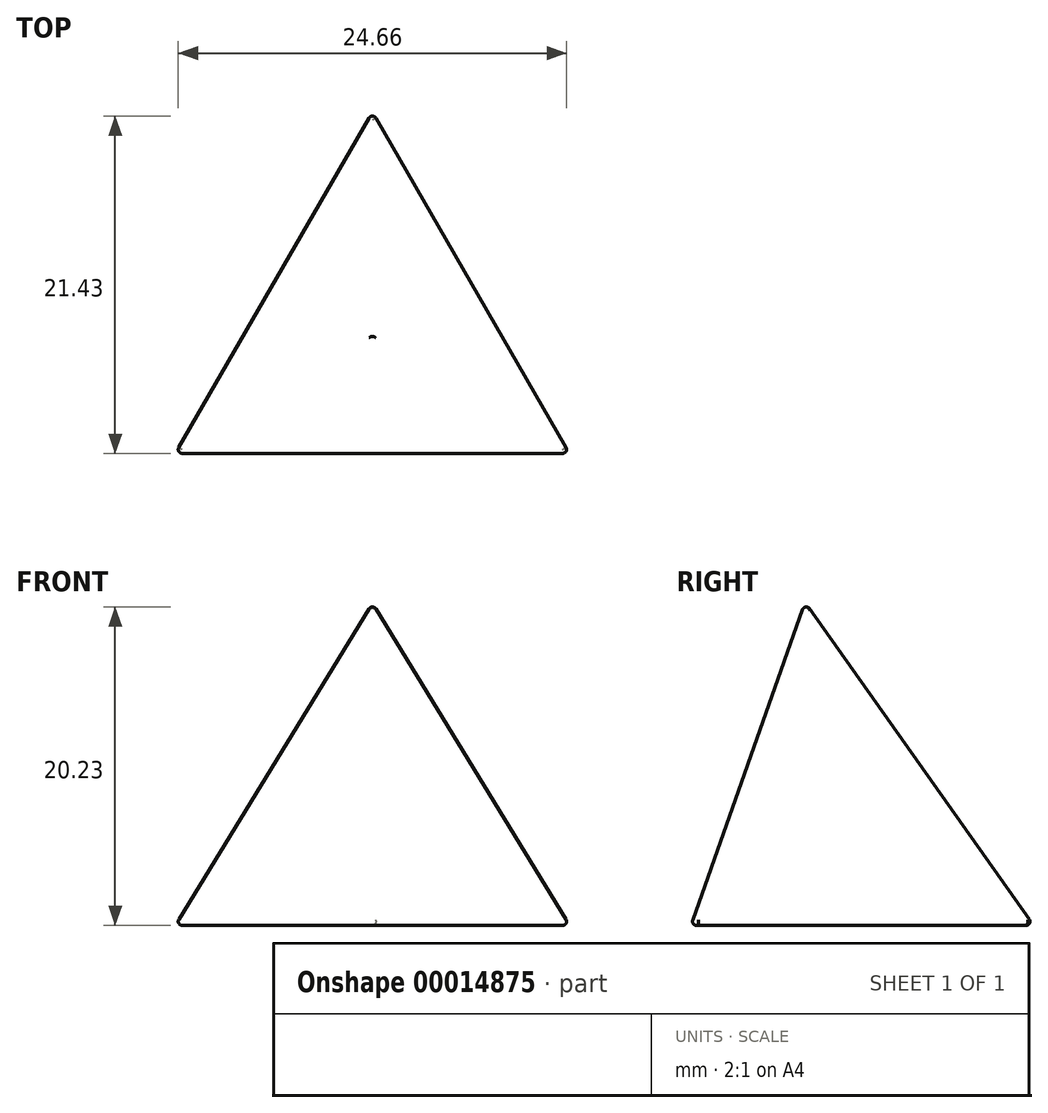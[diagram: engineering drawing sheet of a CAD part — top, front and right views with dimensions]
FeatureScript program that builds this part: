
annotation { "Feature Type Name" : "Feature", "Feature Type Description" : "" }
export const myFeature = defineFeature(function(context is Context, id is Id, definition is map)
    precondition{}
    {
        {
            var Q0;
            Q0=qCreatedBy(makeId("Top.planeOp"),FACE);
            var sketch = newSketch(context, id + "F0", { "sketchPlane" : qUnion([Q0])});
            skLineSegment(sketch, "E0", {"start": v(-12.7, -7.33) * mm, "end": v(12.7, -7.33) * mm, "construction": true});
            skLineSegment(sketch, "E1", {"start": v(12.7, -7.33) * mm, "end": v(0, 14.66) * mm, "construction": true});
            skLineSegment(sketch, "E2", {"start": v(0, 14.66) * mm, "end": v(-12.7, -7.33) * mm, "construction": true});
            skCircle(sketch, "E3", {"center": v(0, 0) * mm, "radius": 14.66 * mm});
            skLineSegment(sketch, "E4", {"start": v(-12.7, -7.33) * mm, "end": v(0, 0) * mm, "construction": true});
            skCircle(sketch, "E5", {"center": v(-12.7, -7.33) * mm, "radius": 25.4 * mm, "construction": true});
            skLineSegment(sketch, "E6", {"start": v(-12.7, -7.33) * mm, "end": v(-34.7, -20.03) * mm, "construction": true});
            skSolve(sketch);
        }
        {
            var Q0;
            Q0=sQuery(id+"F0.wireOp",EDGE,"E4");
            cPlane(context, id + "F1", {"entities" : qUnion([Q0]), "cplaneType" : CPlaneType.LINE_ANGLE, "offset" : 152.4 * mm, "angle" : 0 * degree, "width" : 152.4 * mm, "height" : 152.4 * mm});
        }
        {
            var Q0;
            Q0=qCreatedBy(id+"F1.planeOp",FACE);
            var sketch = newSketch(context, id + "F2", { "sketchPlane" : qUnion([Q0])});
            skLineSegment(sketch, "E7", {"start": v(14.66, 0) * mm, "end": v(0, 20.74) * mm, "construction": true});
            skLineSegment(sketch, "E8", {"start": v(0, 20.74) * mm, "end": v(0, 0) * mm, "construction": true});
            skSolve(sketch);
        }
        {
            var Q0;
            Q0=sQuery(id+"F0.wireOp",VERTEX,"E1.end");
            var Q1;
            Q1=sQuery(id+"F0.wireOp",VERTEX,"E2.end");
            var Q2;
            Q2=sQuery(id+"F2.wireOp",VERTEX,"E7.end");
            cPlane(context, id + "F3", {"entities" : qUnion([Q0, Q1, Q2]), "cplaneType" : CPlaneType.THREE_POINT, "offset" : 152.4 * mm, "width" : 152.4 * mm, "height" : 152.4 * mm});
        }
        {
            var Q0;
            Q0=qCreatedBy(id+"F3.planeOp",FACE);
            var sketch = newSketch(context, id + "F4", { "sketchPlane" : qUnion([Q0])});
            skCircle(sketch, "E9", {"center": v(-0.92, 4.8) * mm, "radius": 14.66 * mm});
            skSolve(sketch);
        }
        {
            var Q0;
            Q0=sQuery(id+"F0.wireOp",VERTEX,"E2.start");
            var Q1;
            Q1=sQuery(id+"F0.wireOp",VERTEX,"E0.end");
            var Q2;
            Q2=sQuery(id+"F2.wireOp",VERTEX,"E7.end");
            cPlane(context, id + "F5", {"entities" : qUnion([Q0, Q1, Q2]), "cplaneType" : CPlaneType.THREE_POINT, "offset" : 152.4 * mm, "width" : 152.4 * mm, "height" : 152.4 * mm});
        }
        {
            var Q0;
            Q0=qCreatedBy(id+"F5.planeOp",FACE);
            var sketch = newSketch(context, id + "F6", { "sketchPlane" : qUnion([Q0])});
            skCircle(sketch, "E10", {"center": v(-0.92, 4.8) * mm, "radius": 14.66 * mm});
            skSolve(sketch);
        }
        {
            var Q0;
            Q0=sQuery(id+"F0.wireOp",VERTEX,"E2.end");
            var Q1;
            Q1=sQuery(id+"F2.wireOp",VERTEX,"E7.end");
            var Q2;
            Q2=sQuery(id+"F0.wireOp",VERTEX,"E0.end");
            cPlane(context, id + "F7", {"entities" : qUnion([Q0, Q1, Q2]), "cplaneType" : CPlaneType.THREE_POINT, "offset" : 152.4 * mm, "width" : 152.4 * mm, "height" : 152.4 * mm});
        }
        {
            var Q0;
            Q0=qCreatedBy(id+"F7.planeOp",FACE);
            var sketch = newSketch(context, id + "F8", { "sketchPlane" : qUnion([Q0])});
            skCircle(sketch, "E11", {"center": v(0, 4.89) * mm, "radius": 14.66 * mm});
            skSolve(sketch);
        }
        {
            var Q0;
            Q0=sQuery(id+"F2.wireOp",VERTEX,"E7.start");
            var Q1;
            Q1=sQuery(id+"F6.wireOp",VERTEX,"E10.center");
            var Q2;
            Q2=sQuery(id+"F2.wireOp",VERTEX,"E7.end");
            cPlane(context, id + "F9", {"entities" : qUnion([Q0, Q1, Q2]), "cplaneType" : CPlaneType.THREE_POINT, "offset" : 152.4 * mm, "width" : 152.4 * mm, "height" : 152.4 * mm});
        }
        {
            var Q0;
            Q0=qCreatedBy(id+"F9.planeOp",FACE);
            var sketch = newSketch(context, id + "F10", { "sketchPlane" : qUnion([Q0])});
            skLineSegment(sketch, "E12", {"start": v(14.66, 0) * mm, "end": v(-4.89, 6.91) * mm});
            skPoint(sketch, "E13", {"position": v(0, 5.18) * mm});
            skArc(sketch, "E14", {"start": v(14.66, 0) * mm, "mid": v(5.18, 19.85) * mm, "end": v(-14.66, 10.37) * mm});
            skLineSegment(sketch, "E15", {"start": v(-4.89, 6.91) * mm, "end": v(-14.66, 10.37) * mm});
            skSolve(sketch);
        }
        {
            var Q0;
            Q0=makeQuery(id+"F10.imprint","IMPRINT",FACE,{"disambiguationData":[TD([[makeQuery(id+"F10.imprint","IMPRINT",EDGE,{"derivedFrom":sQuery(id+"F10.wireOp",EDGE,"E12")}),-1.0]])]});
            var Q1;
            Q1=sQuery(id+"F10.wireOp",EDGE,"E12");
            revolve(context, id + "F11", {"entities" : qUnion([Q0]), "axis" : qUnion([Q1]), "revolveType" : RevolveType.FULL});
        }
        {
            var Q0;
            Q0=makeQuery(id+"F0.imprint","IMPRINT",FACE,{"disambiguationData":[TD([[makeQuery(id+"F0.imprint","IMPRINT",EDGE,{"derivedFrom":sQuery(id+"F0.wireOp",EDGE,"E3")}),1.0]])]});
            extrude(context, id + "F12", {"entities" : qUnion([Q0]), "operationType" : NewBodyOperationType.REMOVE, "endBound" : BoundingType.THROUGH_ALL, "oppositeDirection" : true, "depth" : 25.4 * mm});
        }
        {
            var Q0;
            Q0=makeQuery(id+"F4.imprint","IMPRINT",FACE,{"disambiguationData":[TD([[makeQuery(id+"F4.imprint","IMPRINT",EDGE,{"derivedFrom":sQuery(id+"F4.wireOp",EDGE,"E9")}),1.0]])]});
            extrude(context, id + "F13", {"entities" : qUnion([Q0]), "operationType" : NewBodyOperationType.REMOVE, "endBound" : BoundingType.THROUGH_ALL, "oppositeDirection" : true, "depth" : 25.4 * mm});
        }
        {
            var Q0;
            Q0=makeQuery(id+"F6.imprint","IMPRINT",FACE,{"disambiguationData":[TD([[makeQuery(id+"F6.imprint","IMPRINT",EDGE,{"derivedFrom":sQuery(id+"F6.wireOp",EDGE,"E10")}),1.0]])]});
            extrude(context, id + "F14", {"entities" : qUnion([Q0]), "operationType" : NewBodyOperationType.REMOVE, "endBound" : BoundingType.THROUGH_ALL, "depth" : 25.4 * mm});
        }
        {
            var Q0;
            Q0=makeQuery(id+"F8.imprint","IMPRINT",FACE,{"disambiguationData":[TD([[makeQuery(id+"F8.imprint","IMPRINT",EDGE,{"derivedFrom":sQuery(id+"F8.wireOp",EDGE,"E11")}),1.0]])]});
            extrude(context, id + "F15", {"entities" : qUnion([Q0]), "operationType" : NewBodyOperationType.REMOVE, "endBound" : BoundingType.THROUGH_ALL, "depth" : 25.4 * mm});
        }
        {
            var Q0;
            Q0=makeQuery(id+"F15.boolean.opBoolean","INTERSECT",EDGE,{"derivedFrom":[makeQuery(id+"F14.boolean.opBoolean","COPY",FACE,{"derivedFrom":makeQuery(id+"F14.opExtrude","CAP_FACE",FACE,{"disambiguationData":[OSD([sQuery(id+"F6.wireOp",EDGE,"E10")])],"isStart":true})}),makeQuery(id+"F15.opExtrude","CAP_FACE",FACE,{"disambiguationData":[OSD([sQuery(id+"F8.wireOp",EDGE,"E11")])],"isStart":true})]});
            var Q1;
            Q1=makeQuery(id+"F15.boolean.opBoolean","INTERSECT",EDGE,{"derivedFrom":[makeQuery(id+"F13.boolean.opBoolean","COPY",FACE,{"derivedFrom":makeQuery(id+"F13.opExtrude","CAP_FACE",FACE,{"disambiguationData":[OSD([sQuery(id+"F4.wireOp",EDGE,"E9")])],"isStart":true})}),makeQuery(id+"F15.opExtrude","CAP_FACE",FACE,{"disambiguationData":[OSD([sQuery(id+"F8.wireOp",EDGE,"E11")])],"isStart":true})]});
            var Q2;
            Q2=makeQuery(id+"F15.boolean.opBoolean","INTERSECT",EDGE,{"derivedFrom":[makeQuery(id+"F12.boolean.opBoolean","COPY",FACE,{"derivedFrom":makeQuery(id+"F12.opExtrude","CAP_FACE",FACE,{"disambiguationData":[OSD([sQuery(id+"F0.wireOp",EDGE,"E3")])],"isStart":true})}),makeQuery(id+"F15.opExtrude","CAP_FACE",FACE,{"disambiguationData":[OSD([sQuery(id+"F8.wireOp",EDGE,"E11")])],"isStart":true})]});
            var Q3;
            Q3=makeQuery(id+"F13.boolean.opBoolean","INTERSECT",EDGE,{"derivedFrom":[makeQuery(id+"F12.boolean.opBoolean","COPY",FACE,{"derivedFrom":makeQuery(id+"F12.opExtrude","CAP_FACE",FACE,{"disambiguationData":[OSD([sQuery(id+"F0.wireOp",EDGE,"E3")])],"isStart":true})}),makeQuery(id+"F13.opExtrude","CAP_FACE",FACE,{"disambiguationData":[OSD([sQuery(id+"F4.wireOp",EDGE,"E9")])],"isStart":true})]});
            var Q4;
            Q4=makeQuery(id+"F14.boolean.opBoolean","INTERSECT",EDGE,{"derivedFrom":[makeQuery(id+"F13.boolean.opBoolean","COPY",FACE,{"derivedFrom":makeQuery(id+"F13.opExtrude","CAP_FACE",FACE,{"disambiguationData":[OSD([sQuery(id+"F4.wireOp",EDGE,"E9")])],"isStart":true})}),makeQuery(id+"F14.opExtrude","CAP_FACE",FACE,{"disambiguationData":[OSD([sQuery(id+"F6.wireOp",EDGE,"E10")])],"isStart":true})]});
            var Q5;
            Q5=makeQuery(id+"F14.boolean.opBoolean","INTERSECT",EDGE,{"derivedFrom":[makeQuery(id+"F12.boolean.opBoolean","COPY",FACE,{"derivedFrom":makeQuery(id+"F12.opExtrude","CAP_FACE",FACE,{"disambiguationData":[OSD([sQuery(id+"F0.wireOp",EDGE,"E3")])],"isStart":true})}),makeQuery(id+"F14.opExtrude","CAP_FACE",FACE,{"disambiguationData":[OSD([sQuery(id+"F6.wireOp",EDGE,"E10")])],"isStart":true})]});
            fillet(context, id + "F16", {"entities" : qUnion([Q0, Q1, Q2, Q3, Q4, Q5]), "radius" : 0.25 * mm, "tangentPropagation" : true, "allowEdgeOverflow" : false});
        }
    });
